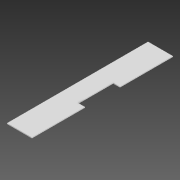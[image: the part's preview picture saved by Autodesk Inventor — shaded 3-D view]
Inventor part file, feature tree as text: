
AUTODESK INVENTOR PART (.ipt)
format: ipt  version: 2020 (Build 240168000, 168)  size: 82,944 bytes
history: native  units: in
note: dims shown in document units (in); Inventor stores cm internally (conversion verified against a paired STEP export)
features: extrude x1, sketch x1
ambient origin geometry x8: Origin, YZ Plane, XZ Plane, XY Plane, X Axis, Y Axis, Z Axis, Center Point
bodies: Solid1 (feature_tree)
feature tree (2):
  extrude  "Extrusion1"  Depth=24.6063in
  sketch  "Sketch1"  dims[d0=4.3307in d1=24.6063in d2=1.1811in d3=3.0709in d4=6.1417in d5=0.1181in d6=0.0in]
